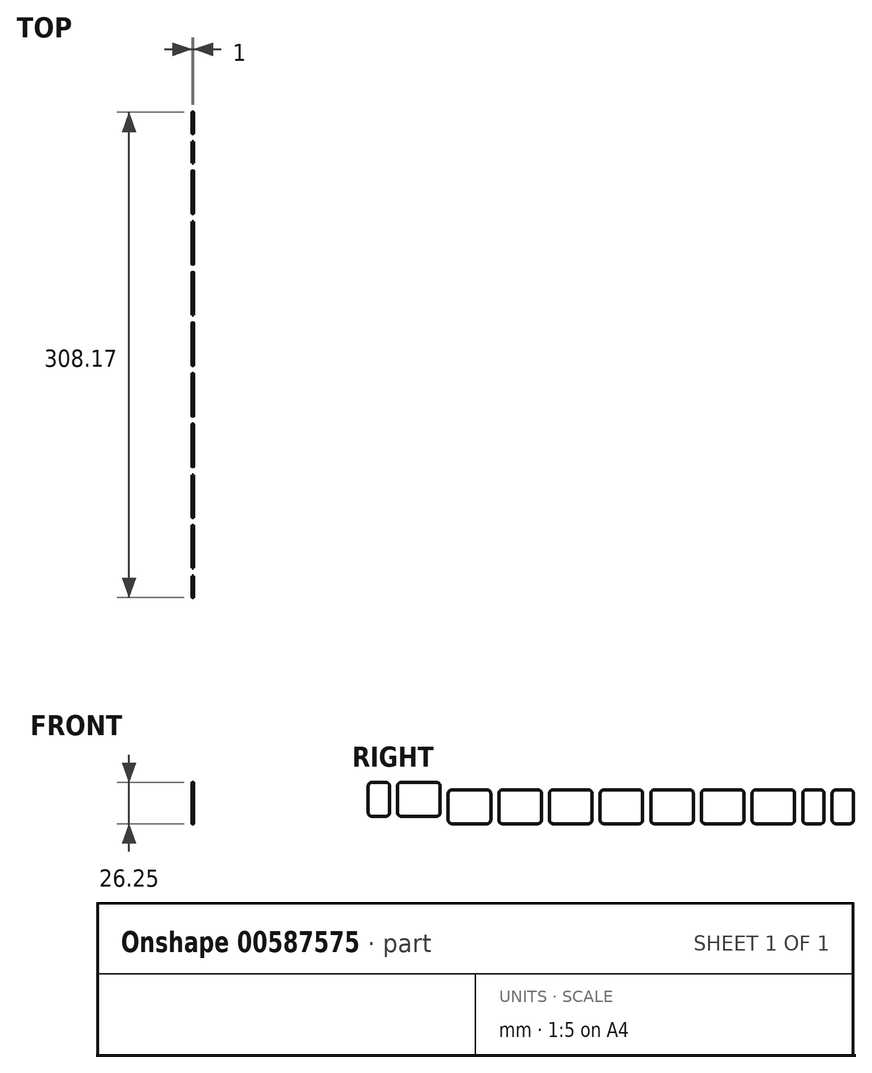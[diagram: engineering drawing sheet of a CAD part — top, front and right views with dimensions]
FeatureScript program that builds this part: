
annotation { "Feature Type Name" : "Feature", "Feature Type Description" : "" }
export const myFeature = defineFeature(function(context is Context, id is Id, definition is map)
    precondition{}
    {
        {
            var Q0;
            Q0=qCreatedBy(makeId("Right.planeOp"),FACE);
            var sketch = newSketch(context, id + "F0", { "sketchPlane" : qUnion([Q0])});
            skPoint(sketch, "E0.visualSharp", {"position": v(-157.96, 10.13) * mm});
            skPoint(sketch, "E1.visualSharp", {"position": v(-144.96, 10.13) * mm});
            skPoint(sketch, "E2.visualSharp", {"position": v(-157.96, -10.87) * mm});
            skPoint(sketch, "E3.visualSharp", {"position": v(-144.96, -10.87) * mm});
            skPoint(sketch, "E4.visualSharp", {"position": v(-139.3, -10.87) * mm});
            skPoint(sketch, "E5.visualSharp", {"position": v(-139.3, 10.13) * mm});
            skPoint(sketch, "E6.visualSharp", {"position": v(-112.8, 10.13) * mm});
            skPoint(sketch, "E7.visualSharp", {"position": v(-112.8, -10.87) * mm});
            skPoint(sketch, "E8.oppositeSnap0", {"position": v(-61.71, -15.62) * mm});
            skPoint(sketch, "E9.visualSharp", {"position": v(-107.13, 5.38) * mm});
            skPoint(sketch, "E10.visualSharp", {"position": v(-80.63, 5.38) * mm});
            skPoint(sketch, "E11.visualSharp", {"position": v(-74.96, 5.38) * mm});
            skPoint(sketch, "E12.visualSharp", {"position": v(-48.46, 5.38) * mm});
            skPoint(sketch, "E13.visualSharp", {"position": v(-42.8, 5.38) * mm});
            skPoint(sketch, "E14.visualSharp", {"position": v(-16.3, 5.38) * mm});
            skPoint(sketch, "E15.visualSharp", {"position": v(-10.63, 5.38) * mm});
            skPoint(sketch, "E16.visualSharp", {"position": v(15.87, 5.38) * mm});
            skPoint(sketch, "E17.visualSharp", {"position": v(21.54, 5.38) * mm});
            skPoint(sketch, "E18.visualSharp", {"position": v(48.04, 5.38) * mm});
            skPoint(sketch, "E19.visualSharp", {"position": v(53.7, 5.38) * mm});
            skPoint(sketch, "E20.visualSharp", {"position": v(80.2, 5.38) * mm});
            skPoint(sketch, "E21.visualSharp", {"position": v(85.87, 5.38) * mm});
            skPoint(sketch, "E22.visualSharp", {"position": v(112.37, 5.38) * mm});
            skPoint(sketch, "E23.visualSharp", {"position": v(118.04, 5.38) * mm});
            skPoint(sketch, "E24.visualSharp", {"position": v(131.04, 5.38) * mm});
            skPoint(sketch, "E25.visualSharp", {"position": v(136.7, 5.38) * mm});
            skPoint(sketch, "E26.visualSharp", {"position": v(149.7, 5.38) * mm});
            skPoint(sketch, "E27.visualSharp", {"position": v(149.7, -15.62) * mm});
            skPoint(sketch, "E28.visualSharp", {"position": v(136.7, -15.62) * mm});
            skPoint(sketch, "E29.visualSharp", {"position": v(131.04, -15.62) * mm});
            skPoint(sketch, "E30.visualSharp", {"position": v(118.04, -15.62) * mm});
            skPoint(sketch, "E31.visualSharp", {"position": v(112.37, -15.62) * mm});
            skPoint(sketch, "E32.visualSharp", {"position": v(85.87, -15.62) * mm});
            skPoint(sketch, "E33.visualSharp", {"position": v(80.2, -15.62) * mm});
            skPoint(sketch, "E34.visualSharp", {"position": v(53.7, -15.62) * mm});
            skPoint(sketch, "E35.visualSharp", {"position": v(48.04, -15.62) * mm});
            skPoint(sketch, "E36.visualSharp", {"position": v(21.54, -15.62) * mm});
            skPoint(sketch, "E37.visualSharp", {"position": v(15.87, -15.62) * mm});
            skPoint(sketch, "E38.visualSharp", {"position": v(-10.63, -15.62) * mm});
            skPoint(sketch, "E39.visualSharp", {"position": v(-16.3, -15.62) * mm});
            skPoint(sketch, "E40.visualSharp", {"position": v(-42.8, -15.62) * mm});
            skPoint(sketch, "E41.visualSharp", {"position": v(-48.46, -15.62) * mm});
            skPoint(sketch, "E42.visualSharp", {"position": v(-74.96, -15.62) * mm});
            skPoint(sketch, "E43.visualSharp", {"position": v(-80.63, -15.62) * mm});
            skPoint(sketch, "E44.visualSharp", {"position": v(-107.13, -15.62) * mm});
            skArc(sketch, "E45.0", {"start": v(-155.96, 10.38) * mm, "mid": v(-157.55, 9.72) * mm, "end": v(-158.21, 8.13) * mm});
            skLineSegment(sketch, "E45.1", {"start": v(-158.21, 8.13) * mm, "end": v(-158.21, -8.87) * mm});
            skLineSegment(sketch, "E45.2", {"start": v(-155.96, 10.38) * mm, "end": v(-146.96, 10.38) * mm});
            skArc(sketch, "E45.3", {"start": v(-158.21, -8.87) * mm, "mid": v(-157.55, -10.46) * mm, "end": v(-155.96, -11.12) * mm});
            skArc(sketch, "E45.4", {"start": v(-144.71, 8.13) * mm, "mid": v(-145.37, 9.72) * mm, "end": v(-146.96, 10.38) * mm});
            skLineSegment(sketch, "E45.5", {"start": v(-144.71, 8.13) * mm, "end": v(-144.71, -8.87) * mm});
            skArc(sketch, "E45.6", {"start": v(-146.96, -11.12) * mm, "mid": v(-145.37, -10.46) * mm, "end": v(-144.71, -8.87) * mm});
            skLineSegment(sketch, "E45.7", {"start": v(-155.96, -11.12) * mm, "end": v(-146.96, -11.12) * mm});
            skArc(sketch, "E46.0", {"start": v(-112.54, 8.13) * mm, "mid": v(-113.2, 9.72) * mm, "end": v(-114.8, 10.38) * mm});
            skLineSegment(sketch, "E46.1", {"start": v(-137.3, 10.38) * mm, "end": v(-114.8, 10.38) * mm});
            skLineSegment(sketch, "E46.2", {"start": v(-112.54, 8.13) * mm, "end": v(-112.54, -8.87) * mm});
            skArc(sketch, "E46.3", {"start": v(-137.3, 10.38) * mm, "mid": v(-138.88, 9.72) * mm, "end": v(-139.54, 8.13) * mm});
            skArc(sketch, "E46.4", {"start": v(-114.8, -11.12) * mm, "mid": v(-113.2, -10.46) * mm, "end": v(-112.54, -8.87) * mm});
            skLineSegment(sketch, "E46.5", {"start": v(-137.3, -11.12) * mm, "end": v(-114.8, -11.12) * mm});
            skArc(sketch, "E46.6", {"start": v(-139.54, -8.87) * mm, "mid": v(-138.88, -10.46) * mm, "end": v(-137.3, -11.12) * mm});
            skLineSegment(sketch, "E46.7", {"start": v(-139.54, 8.13) * mm, "end": v(-139.54, -8.87) * mm});
            skArc(sketch, "E47.0", {"start": v(-107.38, -13.62) * mm, "mid": v(-106.72, -15.2) * mm, "end": v(-105.13, -15.87) * mm});
            skLineSegment(sketch, "E47.1", {"start": v(-107.38, 3.38) * mm, "end": v(-107.38, -13.62) * mm});
            skLineSegment(sketch, "E47.2", {"start": v(-105.13, -15.87) * mm, "end": v(-82.63, -15.87) * mm});
            skArc(sketch, "E47.3", {"start": v(-105.13, 5.63) * mm, "mid": v(-106.72, 4.97) * mm, "end": v(-107.38, 3.38) * mm});
            skArc(sketch, "E47.4", {"start": v(-82.63, -15.87) * mm, "mid": v(-81.04, -15.2) * mm, "end": v(-80.38, -13.62) * mm});
            skLineSegment(sketch, "E47.5", {"start": v(-80.38, 3.38) * mm, "end": v(-80.38, -13.62) * mm});
            skArc(sketch, "E47.6", {"start": v(-80.38, 3.38) * mm, "mid": v(-81.04, 4.97) * mm, "end": v(-82.63, 5.63) * mm});
            skLineSegment(sketch, "E47.7", {"start": v(-105.13, 5.63) * mm, "end": v(-82.63, 5.63) * mm});
            skArc(sketch, "E48.0", {"start": v(-72.96, 5.63) * mm, "mid": v(-74.55, 4.97) * mm, "end": v(-75.21, 3.38) * mm});
            skLineSegment(sketch, "E48.1", {"start": v(-75.21, 3.38) * mm, "end": v(-75.21, -13.62) * mm});
            skLineSegment(sketch, "E48.2", {"start": v(-72.96, 5.63) * mm, "end": v(-50.46, 5.63) * mm});
            skArc(sketch, "E48.3", {"start": v(-75.21, -13.62) * mm, "mid": v(-74.55, -15.2) * mm, "end": v(-72.96, -15.87) * mm});
            skArc(sketch, "E48.4", {"start": v(-48.21, 3.38) * mm, "mid": v(-48.87, 4.97) * mm, "end": v(-50.46, 5.63) * mm});
            skLineSegment(sketch, "E48.5", {"start": v(-48.21, 3.38) * mm, "end": v(-48.21, -13.62) * mm});
            skArc(sketch, "E48.6", {"start": v(-50.46, -15.87) * mm, "mid": v(-48.87, -15.2) * mm, "end": v(-48.21, -13.62) * mm});
            skLineSegment(sketch, "E48.7", {"start": v(-72.96, -15.87) * mm, "end": v(-50.46, -15.87) * mm});
            skArc(sketch, "E49.0", {"start": v(-16.05, 3.38) * mm, "mid": v(-16.7, 4.97) * mm, "end": v(-18.3, 5.63) * mm});
            skLineSegment(sketch, "E49.1", {"start": v(-40.8, 5.63) * mm, "end": v(-18.3, 5.63) * mm});
            skLineSegment(sketch, "E49.2", {"start": v(-16.05, 3.38) * mm, "end": v(-16.05, -13.62) * mm});
            skArc(sketch, "E49.3", {"start": v(-40.8, 5.63) * mm, "mid": v(-42.39, 4.97) * mm, "end": v(-43.05, 3.38) * mm});
            skArc(sketch, "E49.4", {"start": v(-18.3, -15.87) * mm, "mid": v(-16.7, -15.2) * mm, "end": v(-16.05, -13.62) * mm});
            skLineSegment(sketch, "E49.5", {"start": v(-40.8, -15.87) * mm, "end": v(-18.3, -15.87) * mm});
            skArc(sketch, "E49.6", {"start": v(-43.05, -13.62) * mm, "mid": v(-42.39, -15.2) * mm, "end": v(-40.8, -15.87) * mm});
            skLineSegment(sketch, "E49.7", {"start": v(-43.05, 3.38) * mm, "end": v(-43.05, -13.62) * mm});
            skArc(sketch, "E50.0", {"start": v(-8.63, 5.63) * mm, "mid": v(-10.22, 4.97) * mm, "end": v(-10.88, 3.38) * mm});
            skLineSegment(sketch, "E50.1", {"start": v(-8.63, 5.63) * mm, "end": v(13.87, 5.63) * mm});
            skLineSegment(sketch, "E50.2", {"start": v(-10.88, 3.38) * mm, "end": v(-10.88, -13.62) * mm});
            skArc(sketch, "E50.3", {"start": v(16.12, 3.38) * mm, "mid": v(15.46, 4.97) * mm, "end": v(13.87, 5.63) * mm});
            skArc(sketch, "E50.4", {"start": v(-10.88, -13.62) * mm, "mid": v(-10.22, -15.2) * mm, "end": v(-8.63, -15.87) * mm});
            skLineSegment(sketch, "E50.5", {"start": v(-8.63, -15.87) * mm, "end": v(13.87, -15.87) * mm});
            skArc(sketch, "E50.6", {"start": v(13.87, -15.87) * mm, "mid": v(15.46, -15.2) * mm, "end": v(16.12, -13.62) * mm});
            skLineSegment(sketch, "E50.7", {"start": v(16.12, 3.38) * mm, "end": v(16.12, -13.62) * mm});
            skArc(sketch, "E51.0", {"start": v(48.29, 3.38) * mm, "mid": v(47.63, 4.97) * mm, "end": v(46.04, 5.63) * mm});
            skLineSegment(sketch, "E51.1", {"start": v(23.54, 5.63) * mm, "end": v(46.04, 5.63) * mm});
            skLineSegment(sketch, "E51.2", {"start": v(48.29, 3.38) * mm, "end": v(48.29, -13.62) * mm});
            skArc(sketch, "E51.3", {"start": v(23.54, 5.63) * mm, "mid": v(21.95, 4.97) * mm, "end": v(21.29, 3.38) * mm});
            skArc(sketch, "E51.4", {"start": v(46.04, -15.87) * mm, "mid": v(47.63, -15.2) * mm, "end": v(48.29, -13.62) * mm});
            skLineSegment(sketch, "E51.5", {"start": v(23.54, -15.87) * mm, "end": v(46.04, -15.87) * mm});
            skArc(sketch, "E51.6", {"start": v(21.29, -13.62) * mm, "mid": v(21.95, -15.2) * mm, "end": v(23.54, -15.87) * mm});
            skLineSegment(sketch, "E51.7", {"start": v(21.29, 3.38) * mm, "end": v(21.29, -13.62) * mm});
            skArc(sketch, "E52.0", {"start": v(80.45, 3.38) * mm, "mid": v(79.8, 4.97) * mm, "end": v(78.2, 5.63) * mm});
            skLineSegment(sketch, "E52.1", {"start": v(55.7, 5.63) * mm, "end": v(78.2, 5.63) * mm});
            skLineSegment(sketch, "E52.2", {"start": v(80.45, 3.38) * mm, "end": v(80.45, -13.62) * mm});
            skArc(sketch, "E52.3", {"start": v(55.7, 5.63) * mm, "mid": v(54.11, 4.97) * mm, "end": v(53.45, 3.38) * mm});
            skArc(sketch, "E52.4", {"start": v(78.2, -15.87) * mm, "mid": v(79.8, -15.2) * mm, "end": v(80.45, -13.62) * mm});
            skLineSegment(sketch, "E52.5", {"start": v(55.7, -15.87) * mm, "end": v(78.2, -15.87) * mm});
            skArc(sketch, "E52.6", {"start": v(53.45, -13.62) * mm, "mid": v(54.11, -15.2) * mm, "end": v(55.7, -15.87) * mm});
            skLineSegment(sketch, "E52.7", {"start": v(53.45, 3.38) * mm, "end": v(53.45, -13.62) * mm});
            skArc(sketch, "E53.0", {"start": v(112.62, 3.38) * mm, "mid": v(111.96, 4.97) * mm, "end": v(110.37, 5.63) * mm});
            skLineSegment(sketch, "E53.1", {"start": v(87.87, 5.63) * mm, "end": v(110.37, 5.63) * mm});
            skLineSegment(sketch, "E53.2", {"start": v(112.62, 3.38) * mm, "end": v(112.62, -13.62) * mm});
            skArc(sketch, "E53.3", {"start": v(87.87, 5.63) * mm, "mid": v(86.28, 4.97) * mm, "end": v(85.62, 3.38) * mm});
            skArc(sketch, "E53.4", {"start": v(110.37, -15.87) * mm, "mid": v(111.96, -15.2) * mm, "end": v(112.62, -13.62) * mm});
            skLineSegment(sketch, "E53.5", {"start": v(87.87, -15.87) * mm, "end": v(110.37, -15.87) * mm});
            skArc(sketch, "E53.6", {"start": v(85.62, -13.62) * mm, "mid": v(86.28, -15.2) * mm, "end": v(87.87, -15.87) * mm});
            skLineSegment(sketch, "E53.7", {"start": v(85.62, 3.38) * mm, "end": v(85.62, -13.62) * mm});
            skArc(sketch, "E54.0", {"start": v(131.29, 3.38) * mm, "mid": v(130.63, 4.97) * mm, "end": v(129.04, 5.63) * mm});
            skLineSegment(sketch, "E54.1", {"start": v(120.04, 5.63) * mm, "end": v(129.04, 5.63) * mm});
            skLineSegment(sketch, "E54.2", {"start": v(131.29, 3.38) * mm, "end": v(131.29, -13.62) * mm});
            skArc(sketch, "E54.3", {"start": v(120.04, 5.63) * mm, "mid": v(118.45, 4.97) * mm, "end": v(117.79, 3.38) * mm});
            skArc(sketch, "E54.4", {"start": v(129.04, -15.87) * mm, "mid": v(130.63, -15.2) * mm, "end": v(131.29, -13.62) * mm});
            skLineSegment(sketch, "E54.5", {"start": v(120.04, -15.87) * mm, "end": v(129.04, -15.87) * mm});
            skArc(sketch, "E54.6", {"start": v(117.79, -13.62) * mm, "mid": v(118.45, -15.2) * mm, "end": v(120.04, -15.87) * mm});
            skLineSegment(sketch, "E54.7", {"start": v(117.79, 3.38) * mm, "end": v(117.79, -13.62) * mm});
            skArc(sketch, "E55.0", {"start": v(138.7, 5.63) * mm, "mid": v(137.11, 4.97) * mm, "end": v(136.46, 3.38) * mm});
            skLineSegment(sketch, "E55.1", {"start": v(138.7, 5.63) * mm, "end": v(147.7, 5.63) * mm});
            skLineSegment(sketch, "E55.2", {"start": v(136.46, 3.38) * mm, "end": v(136.46, -13.62) * mm});
            skArc(sketch, "E55.3", {"start": v(149.96, 3.38) * mm, "mid": v(149.3, 4.97) * mm, "end": v(147.7, 5.63) * mm});
            skArc(sketch, "E55.4", {"start": v(136.46, -13.62) * mm, "mid": v(137.11, -15.2) * mm, "end": v(138.7, -15.87) * mm});
            skLineSegment(sketch, "E55.5", {"start": v(138.7, -15.87) * mm, "end": v(147.7, -15.87) * mm});
            skArc(sketch, "E55.6", {"start": v(147.7, -15.87) * mm, "mid": v(149.3, -15.2) * mm, "end": v(149.96, -13.62) * mm});
            skLineSegment(sketch, "E55.7", {"start": v(149.96, 3.38) * mm, "end": v(149.96, -13.62) * mm});
            skSolve(sketch);
        }
        {
            var Q0;
            Q0=makeQuery(id+"F0.imprint","IMPRINT",FACE,{"disambiguationData":[TD([[makeQuery(id+"F0.imprint","IMPRINT",EDGE,{"derivedFrom":sQuery(id+"F0.wireOp",EDGE,"E52.0")}),1.0]])]});
            var Q1;
            Q1=makeQuery(id+"F0.imprint","IMPRINT",FACE,{"disambiguationData":[TD([[makeQuery(id+"F0.imprint","IMPRINT",EDGE,{"derivedFrom":sQuery(id+"F0.wireOp",EDGE,"E49.0")}),1.0]])]});
            var Q2;
            Q2=makeQuery(id+"F0.imprint","IMPRINT",FACE,{"disambiguationData":[TD([[makeQuery(id+"F0.imprint","IMPRINT",EDGE,{"derivedFrom":sQuery(id+"F0.wireOp",EDGE,"E45.0")}),1.0]])]});
            var Q3;
            Q3=makeQuery(id+"F0.imprint","IMPRINT",FACE,{"disambiguationData":[TD([[makeQuery(id+"F0.imprint","IMPRINT",EDGE,{"derivedFrom":sQuery(id+"F0.wireOp",EDGE,"E47.0")}),1.0]])]});
            var Q4;
            Q4=makeQuery(id+"F0.imprint","IMPRINT",FACE,{"disambiguationData":[TD([[makeQuery(id+"F0.imprint","IMPRINT",EDGE,{"derivedFrom":sQuery(id+"F0.wireOp",EDGE,"E51.0")}),1.0]])]});
            var Q5;
            Q5=makeQuery(id+"F0.imprint","IMPRINT",FACE,{"disambiguationData":[TD([[makeQuery(id+"F0.imprint","IMPRINT",EDGE,{"derivedFrom":sQuery(id+"F0.wireOp",EDGE,"E48.0")}),1.0]])]});
            var Q6;
            Q6=makeQuery(id+"F0.imprint","IMPRINT",FACE,{"disambiguationData":[TD([[makeQuery(id+"F0.imprint","IMPRINT",EDGE,{"derivedFrom":sQuery(id+"F0.wireOp",EDGE,"E50.0")}),1.0]])]});
            var Q7;
            Q7=makeQuery(id+"F0.imprint","IMPRINT",FACE,{"disambiguationData":[TD([[makeQuery(id+"F0.imprint","IMPRINT",EDGE,{"derivedFrom":sQuery(id+"F0.wireOp",EDGE,"E46.0")}),1.0]])]});
            var Q8;
            Q8=makeQuery(id+"F0.imprint","IMPRINT",FACE,{"disambiguationData":[TD([[makeQuery(id+"F0.imprint","IMPRINT",EDGE,{"derivedFrom":sQuery(id+"F0.wireOp",EDGE,"E55.0")}),1.0]])]});
            var Q9;
            Q9=makeQuery(id+"F0.imprint","IMPRINT",FACE,{"disambiguationData":[TD([[makeQuery(id+"F0.imprint","IMPRINT",EDGE,{"derivedFrom":sQuery(id+"F0.wireOp",EDGE,"E53.0")}),1.0]])]});
            var Q10;
            Q10=makeQuery(id+"F0.imprint","IMPRINT",FACE,{"disambiguationData":[TD([[makeQuery(id+"F0.imprint","IMPRINT",EDGE,{"derivedFrom":sQuery(id+"F0.wireOp",EDGE,"E54.0")}),1.0]])]});
            extrude(context, id + "F1", {"entities" : qUnion([Q0, Q1, Q2, Q3, Q4, Q5, Q6, Q7, Q8, Q9, Q10]), "depth" : 1 * mm, "offsetDistance" : 25 * mm});
        }
    });
